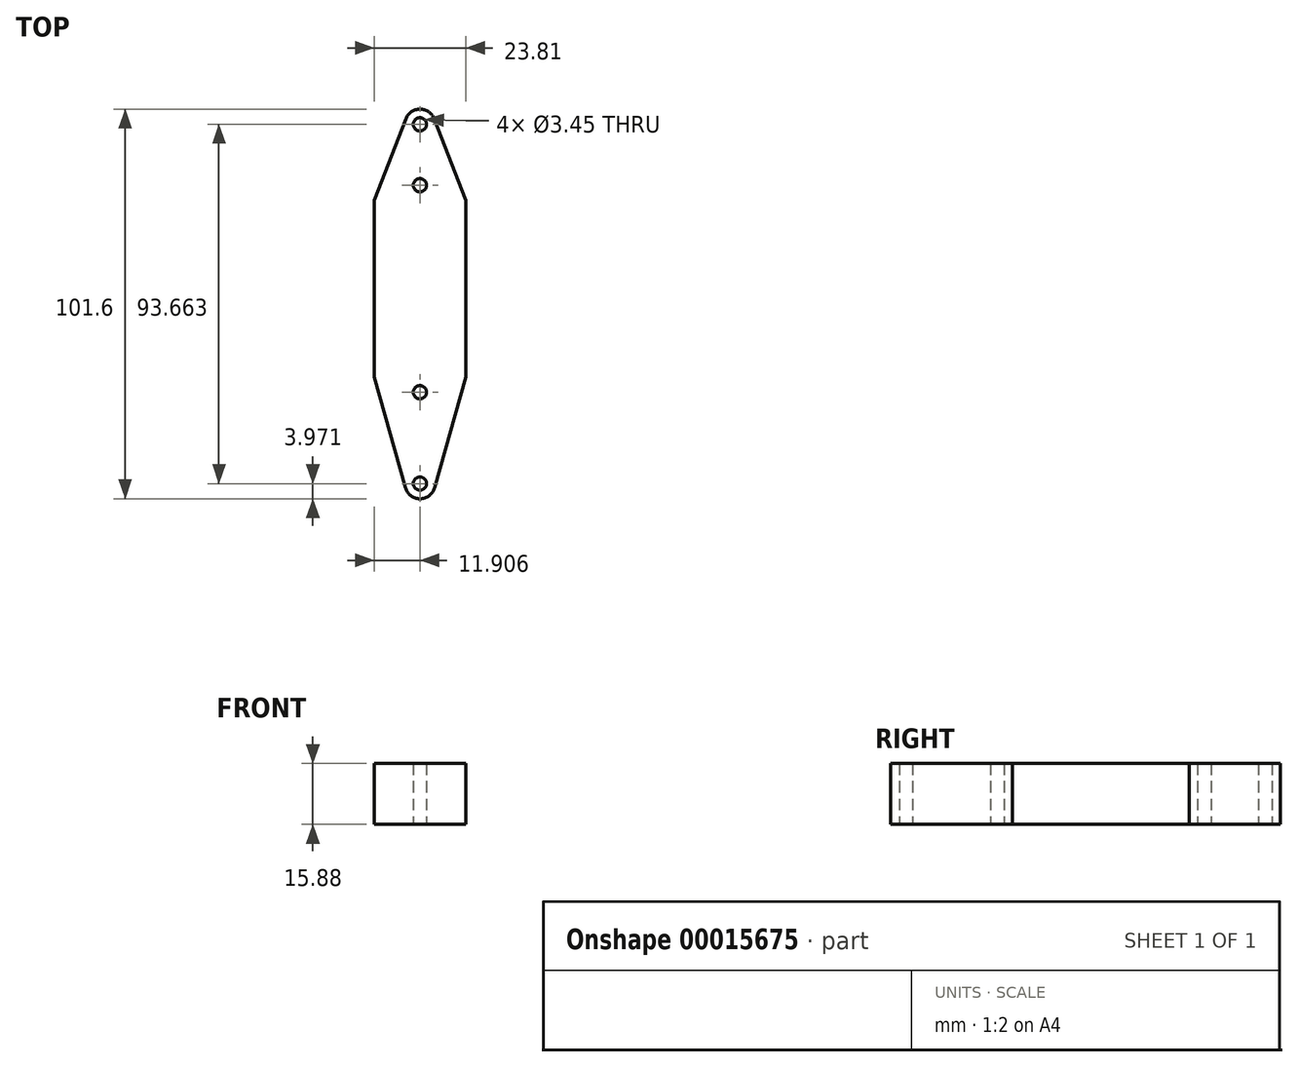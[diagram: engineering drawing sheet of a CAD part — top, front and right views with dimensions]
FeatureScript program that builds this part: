
annotation { "Feature Type Name" : "Feature", "Feature Type Description" : "" }
export const myFeature = defineFeature(function(context is Context, id is Id, definition is map)
    precondition{}
    {
        {
            var Q0;
            Q0=qCreatedBy(makeId("Top.planeOp"),FACE);
            var sketch = newSketch(context, id + "F0", { "sketchPlane" : qUnion([Q0])});
            skLineSegment(sketch, "E0.bottom", {"start": v(0, 0) * mm, "end": v(23.81, 0) * mm, "construction": true});
            skLineSegment(sketch, "E0.top", {"start": v(0, -46.04) * mm, "end": v(23.81, -46.04) * mm, "construction": true});
            skLineSegment(sketch, "E0.left", {"start": v(0, 0) * mm, "end": v(0, -46.04) * mm});
            skLineSegment(sketch, "E0.right", {"start": v(23.81, 0) * mm, "end": v(23.81, -46.04) * mm});
            skLineSegment(sketch, "E1", {"start": v(11.9, -46.04) * mm, "end": v(11.9, -50) * mm});
            skLineSegment(sketch, "E2", {"start": v(11.9, -65.88) * mm, "end": v(11.9, -73.82) * mm});
            skLineSegment(sketch, "E3", {"start": v(11.9, -73.82) * mm, "end": v(11.9, -77.79) * mm});
            skLineSegment(sketch, "E4", {"start": v(0, -46.04) * mm, "end": v(8.08, -74.89) * mm});
            skLineSegment(sketch, "E5", {"start": v(23.81, -46.04) * mm, "end": v(15.73, -74.89) * mm});
            skArc(sketch, "E6", {"start": v(8.08, -74.89) * mm, "mid": v(11.9, -77.79) * mm, "end": v(15.73, -74.89) * mm});
            skCircle(sketch, "E7", {"center": v(11.9, -73.82) * mm, "radius": 1.73 * mm});
            skCircle(sketch, "E8", {"center": v(11.9, -50) * mm, "radius": 1.73 * mm});
            skLineSegment(sketch, "E9", {"start": v(11.9, 0) * mm, "end": v(11.9, 3.97) * mm, "construction": true});
            skLineSegment(sketch, "E10", {"start": v(11.9, 3.97) * mm, "end": v(11.9, 11.9) * mm, "construction": true});
            skLineSegment(sketch, "E11", {"start": v(11.9, 11.9) * mm, "end": v(11.9, 19.84) * mm, "construction": true});
            skLineSegment(sketch, "E12", {"start": v(11.9, 19.84) * mm, "end": v(11.9, 23.81) * mm, "construction": true});
            skArc(sketch, "E13", {"start": v(15.6, 21.27) * mm, "mid": v(11.9, 23.81) * mm, "end": v(8.2, 21.27) * mm});
            skLineSegment(sketch, "E14", {"start": v(0, 0) * mm, "end": v(8.2, 21.27) * mm});
            skLineSegment(sketch, "E15", {"start": v(15.6, 21.27) * mm, "end": v(23.81, 0) * mm});
            skCircle(sketch, "E16", {"center": v(11.9, 19.84) * mm, "radius": 1.73 * mm});
            skCircle(sketch, "E17", {"center": v(11.9, 3.97) * mm, "radius": 1.73 * mm});
            skLineSegment(sketch, "E18", {"start": v(11.9, -65.88) * mm, "end": v(11.9, -57.94) * mm});
            skLineSegment(sketch, "E19", {"start": v(11.9, -57.94) * mm, "end": v(11.9, -50) * mm});
            skSolve(sketch);
        }
        {
            var Q0;
            Q0=qSketchRegion(id+"F0",true);
            extrude(context, id + "F1", {"entities" : qUnion([Q0]), "depth" : 3.97 * mm});
        }
        {
            var Q0;
            Q0=makeQuery(id+"F1.opExtrude","CAP_FACE",FACE,{"disambiguationData":[OSD([sQuery(id+"F0.wireOp",EDGE,"E0.left"),sQuery(id+"F0.wireOp",EDGE,"E0.right"),sQuery(id+"F0.wireOp",EDGE,"f08351e9-1e4a-45c5-8d39-7f6c9946e681"),sQuery(id+"F0.wireOp",EDGE,"b584c3a8-500a-4e4c-a5cf-ec692d5a0e69"),sQuery(id+"F0.wireOp",EDGE,"E4"),sQuery(id+"F0.wireOp",EDGE,"E5"),sQuery(id+"F0.wireOp",EDGE,"E6"),sQuery(id+"F0.wireOp",EDGE,"E7"),sQuery(id+"F0.wireOp",EDGE,"E8"),sQuery(id+"F0.wireOp",EDGE,"E13"),sQuery(id+"F0.wireOp",EDGE,"E14"),sQuery(id+"F0.wireOp",EDGE,"E15"),sQuery(id+"F0.wireOp",EDGE,"E16"),sQuery(id+"F0.wireOp",EDGE,"E17")])],"isStart":false});
            var sketch = newSketch(context, id + "F2", { "sketchPlane" : qUnion([Q0])});
            skLineSegment(sketch, "E20.bottom", {"start": v(0, -46.04) * mm, "end": v(23.81, -46.04) * mm, "construction": true});
            skLineSegment(sketch, "E20.top", {"start": v(0, 0) * mm, "end": v(23.81, 0) * mm, "construction": true});
            skLineSegment(sketch, "E20.left", {"start": v(0, -46.04) * mm, "end": v(0, 0) * mm});
            skLineSegment(sketch, "E20.right", {"start": v(23.81, -46.04) * mm, "end": v(23.81, 0) * mm});
            skLineSegment(sketch, "E21", {"start": v(0, -46.04) * mm, "end": v(8.08, -74.89) * mm});
            skLineSegment(sketch, "E22", {"start": v(15.73, -74.89) * mm, "end": v(23.81, -46.04) * mm});
            skArc(sketch, "E23", {"start": v(8.08, -74.89) * mm, "mid": v(11.9, -77.79) * mm, "end": v(15.73, -74.89) * mm});
            skLineSegment(sketch, "E24", {"start": v(0, 0) * mm, "end": v(8.2, 21.27) * mm});
            skLineSegment(sketch, "E25", {"start": v(23.81, 0) * mm, "end": v(15.6, 21.27) * mm});
            skArc(sketch, "E26", {"start": v(15.6, 21.27) * mm, "mid": v(11.9, 23.81) * mm, "end": v(8.2, 21.27) * mm});
            skSolve(sketch);
        }
        {
            var Q0;
            Q0=makeQuery(id+"F2.imprint","IMPRINT",FACE,{"disambiguationData":[TD([[makeQuery(id+"F2.imprint","IMPRINT",EDGE,{"derivedFrom":sQuery(id+"F2.wireOp",EDGE,"E20.bottom")}),1.0]])]});
            var Q1;
            Q1=makeQuery(id+"F2.imprint","IMPRINT",FACE,{"disambiguationData":[TD([[makeQuery(id+"F2.imprint","IMPRINT",EDGE,{"derivedFrom":sQuery(id+"F2.wireOp",EDGE,"E20.top")}),-1.0]])]});
            var Q2;
            Q2=makeQuery(id+"F2.imprint","IMPRINT",FACE,{"disambiguationData":[TD([[makeQuery(id+"F2.imprint","IMPRINT",EDGE,{"derivedFrom":sQuery(id+"F2.wireOp",EDGE,"E20.left")}),1.0]])]});
            extrude(context, id + "F3", {"entities" : qUnion([Q0, Q1, Q2]), "operationType" : NewBodyOperationType.ADD, "depth" : 11.9 * mm});
        }
    });
